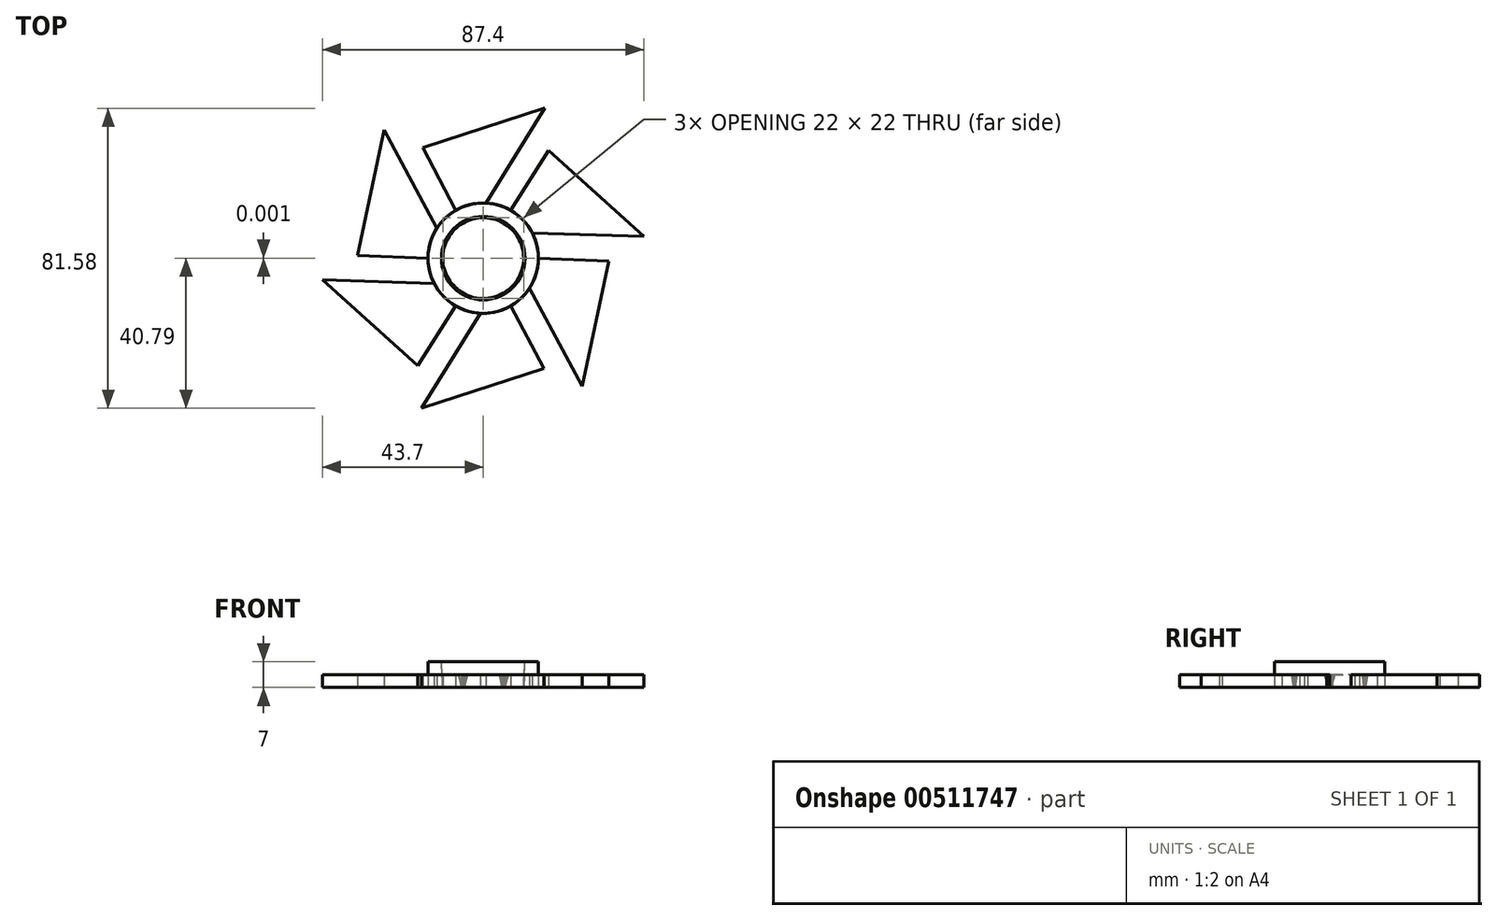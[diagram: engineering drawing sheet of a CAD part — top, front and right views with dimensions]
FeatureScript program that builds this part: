
annotation { "Feature Type Name" : "Feature", "Feature Type Description" : "" }
export const myFeature = defineFeature(function(context is Context, id is Id, definition is map)
    precondition{}
    {
        {
            var Q0;
            Q0=qCreatedBy(makeId("Top.planeOp"),FACE);
            var sketch = newSketch(context, id + "F0", { "sketchPlane" : qUnion([Q0])});
            skCircle(sketch, "E0", {"center": v(0, 0) * mm, "radius": 15 * mm});
            skSolve(sketch);
        }
        {
            var Q0;
            Q0=qCreatedBy(makeId("Top.planeOp"),FACE);
            var sketch = newSketch(context, id + "F1", { "sketchPlane" : qUnion([Q0])});
            skCircle(sketch, "E1", {"center": v(0, 0) * mm, "radius": 11 * mm});
            skSolve(sketch);
        }
        {
            var Q0;
            Q0=qCreatedBy(makeId("Top.planeOp"),FACE);
            var sketch = newSketch(context, id + "F2", { "sketchPlane" : qUnion([Q0])});
            skLineSegment(sketch, "E2", {"start": v(-5.64, 9.44) * mm, "end": v(-16.44, 30) * mm});
            skLineSegment(sketch, "E3", {"start": v(-16.44, 30) * mm, "end": v(16.74, 40.8) * mm});
            skLineSegment(sketch, "E4", {"start": v(16.74, 40.8) * mm, "end": v(0, 13.77) * mm});
            skLineSegment(sketch, "E5", {"start": v(0, 13.77) * mm, "end": v(5.13, 9.74) * mm});
            skLineSegment(sketch, "E6", {"start": v(5.13, 9.74) * mm, "end": v(0, 13.77) * mm});
            skArc(sketch, "E7", {"start": v(5.13, 9.74) * mm, "mid": v(-0.3, 11.53) * mm, "end": v(-5.64, 9.44) * mm});
            skSolve(sketch);
        }
        {
            var Q0;
            Q0=makeQuery(id+"F0.imprint","IMPRINT",FACE,{"disambiguationData":[TD([[makeQuery(id+"F0.imprint","IMPRINT",EDGE,{"derivedFrom":sQuery(id+"F0.wireOp",EDGE,"E0")}),1.0]])]});
            extrude(context, id + "F3", {"entities" : qUnion([Q0]), "depth" : 7 * mm});
        }
        {
            var Q0;
            Q0 = qSketchRegion(id + "F1", true);
            extrude(context, id + "F4", {"entities" : qUnion([Q0]), "operationType" : NewBodyOperationType.REMOVE, "endBound" : BoundingType.THROUGH_ALL, "depth" : 25 * mm, "hasDraft" : true, "draftAngle" : 3 * degree});
        }
        {
            var Q0;
            Q0 = qSketchRegion(id + "F2", true);
            extrude(context, id + "F5", {"entities" : qUnion([Q0]), "operationType" : NewBodyOperationType.ADD, "depth" : (7 / 2) * mm});
        }
        {
            var Q0;
            Q0=makeQuery(id+"F3.opExtrude","SWEPT_BODY",BODY,{"disambiguationData":[OSD([sQuery(id+"F0.wireOp",EDGE,"E0")])]});
            var Q1;
            Q1=makeQuery(id+"F3.opExtrude","CAP_EDGE",EDGE,{"disambiguationData":[OSD([sQuery(id+"F0.wireOp",EDGE,"E0")])],"isStart":false});
            circularPattern(context, id + "F6", {"entities" : qUnion([Q0]), "axis" : qUnion([Q1]), "angle" : 360 * degree, "instanceCount" : 6, "oppositeDirection" : true, "equalSpace" : true});
        }
    });
